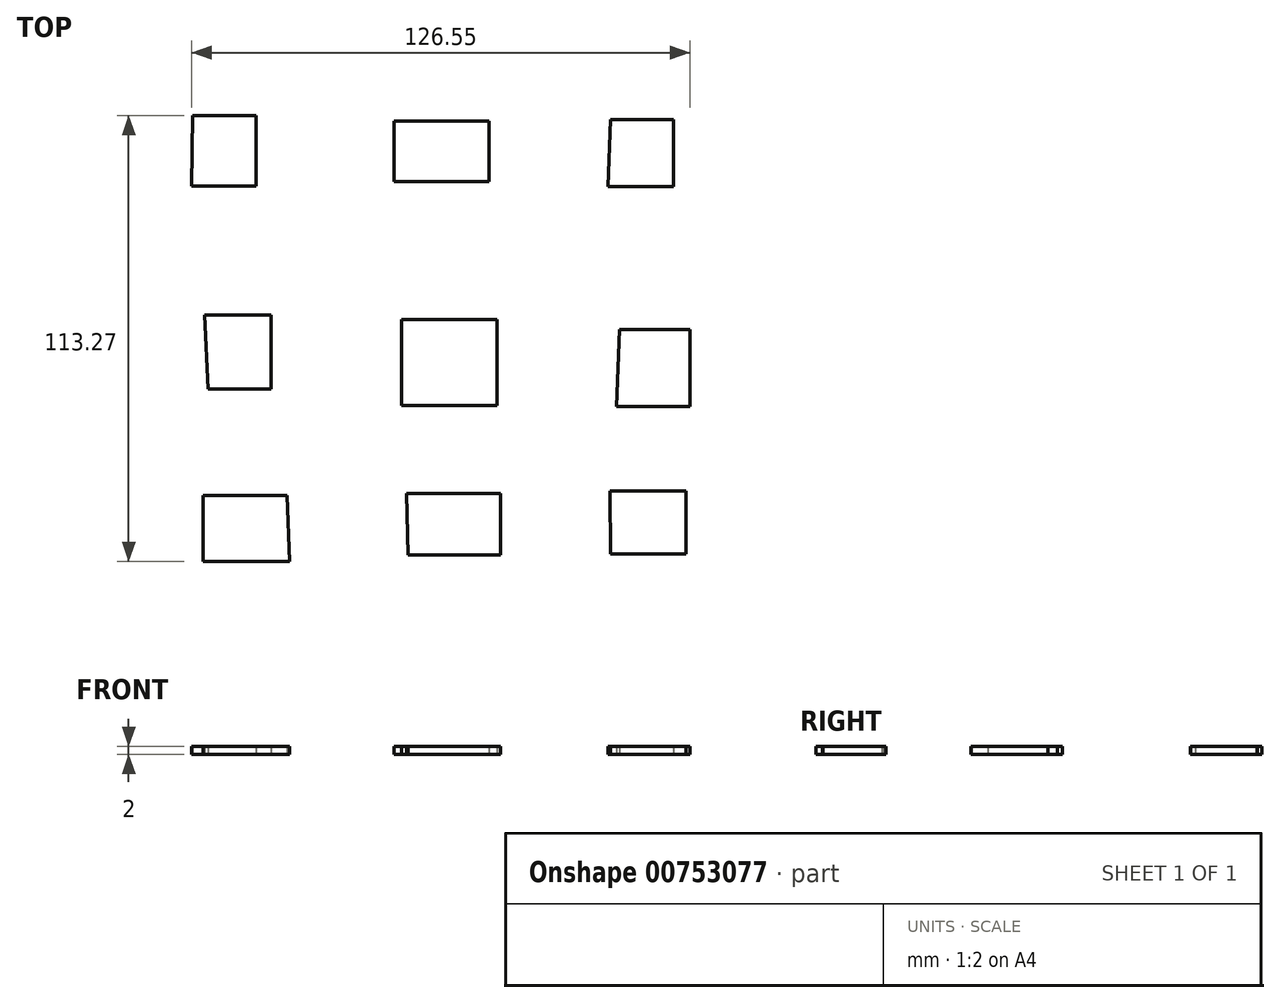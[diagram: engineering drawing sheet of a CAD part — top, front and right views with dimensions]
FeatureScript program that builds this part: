
annotation { "Feature Type Name" : "Feature", "Feature Type Description" : "" }
export const myFeature = defineFeature(function(context is Context, id is Id, definition is map)
    precondition{}
    {
        {
            var Q0;
            Q0=qCreatedBy(makeId("Top.planeOp"),FACE);
            var sketch = newSketch(context, id + "F0", { "sketchPlane" : qUnion([Q0])});
            skLineSegment(sketch, "E0", {"start": v(-64.52, 62.03) * mm, "end": v(-48.34, 62.03) * mm});
            skLineSegment(sketch, "E1", {"start": v(-48.34, 62.03) * mm, "end": v(-48.34, 44.19) * mm});
            skLineSegment(sketch, "E2", {"start": v(-48.34, 44.19) * mm, "end": v(-64.73, 44.19) * mm});
            skLineSegment(sketch, "E3", {"start": v(-64.73, 44.19) * mm, "end": v(-64.52, 62.03) * mm});
            skLineSegment(sketch, "E4", {"start": v(41.7, 61) * mm, "end": v(57.67, 61) * mm});
            skLineSegment(sketch, "E5", {"start": v(57.67, 61) * mm, "end": v(57.67, 43.98) * mm});
            skLineSegment(sketch, "E6", {"start": v(57.67, 43.98) * mm, "end": v(41.08, 43.98) * mm});
            skLineSegment(sketch, "E7", {"start": v(41.08, 43.98) * mm, "end": v(41.7, 61) * mm});
            skLineSegment(sketch, "E8", {"start": v(-13.28, 60.58) * mm, "end": v(10.79, 60.58) * mm});
            skLineSegment(sketch, "E9", {"start": v(10.79, 60.58) * mm, "end": v(10.79, 45.23) * mm});
            skLineSegment(sketch, "E10", {"start": v(10.79, 45.23) * mm, "end": v(-13.28, 45.23) * mm});
            skLineSegment(sketch, "E11", {"start": v(-13.28, 45.23) * mm, "end": v(-13.28, 60.58) * mm});
            skLineSegment(sketch, "E12", {"start": v(-40.45, -34.44) * mm, "end": v(-61.82, -34.44) * mm});
            skLineSegment(sketch, "E13", {"start": v(-61.82, -34.44) * mm, "end": v(-61.82, -51.24) * mm});
            skLineSegment(sketch, "E14", {"start": v(-61.82, -51.24) * mm, "end": v(-39.83, -51.24) * mm});
            skLineSegment(sketch, "E15", {"start": v(-39.83, -51.24) * mm, "end": v(-40.45, -34.44) * mm});
            skLineSegment(sketch, "E16", {"start": v(-10.17, -34.02) * mm, "end": v(13.7, -34.02) * mm});
            skLineSegment(sketch, "E17", {"start": v(13.7, -34.02) * mm, "end": v(13.7, -49.58) * mm});
            skLineSegment(sketch, "E18", {"start": v(13.7, -49.58) * mm, "end": v(-9.75, -49.58) * mm});
            skLineSegment(sketch, "E19", {"start": v(-9.75, -49.58) * mm, "end": v(-10.17, -34.02) * mm});
            skLineSegment(sketch, "E20", {"start": v(41.5, -33.4) * mm, "end": v(60.78, -33.4) * mm});
            skLineSegment(sketch, "E21", {"start": v(60.78, -33.4) * mm, "end": v(60.78, -49.37) * mm});
            skLineSegment(sketch, "E22", {"start": v(60.78, -49.37) * mm, "end": v(41.7, -49.37) * mm});
            skLineSegment(sketch, "E23", {"start": v(41.7, -49.37) * mm, "end": v(41.5, -33.4) * mm});
            skLineSegment(sketch, "E24", {"start": v(-11.41, 10.17) * mm, "end": v(12.86, 10.17) * mm});
            skLineSegment(sketch, "E25", {"start": v(12.86, 10.17) * mm, "end": v(12.86, -11.62) * mm});
            skLineSegment(sketch, "E26", {"start": v(12.86, -11.62) * mm, "end": v(-11.41, -11.62) * mm});
            skLineSegment(sketch, "E27", {"start": v(-11.41, -11.62) * mm, "end": v(-11.41, 10.17) * mm});
            skLineSegment(sketch, "E28", {"start": v(-61.4, 11.41) * mm, "end": v(-44.6, 11.41) * mm});
            skLineSegment(sketch, "E29", {"start": v(-44.6, 11.41) * mm, "end": v(-44.6, -7.47) * mm});
            skLineSegment(sketch, "E30", {"start": v(-44.6, -7.47) * mm, "end": v(-60.58, -7.47) * mm});
            skLineSegment(sketch, "E31", {"start": v(-60.58, -7.47) * mm, "end": v(-61.4, 11.41) * mm});
            skLineSegment(sketch, "E32", {"start": v(43.98, 7.68) * mm, "end": v(61.82, 7.68) * mm});
            skLineSegment(sketch, "E33", {"start": v(61.82, 7.68) * mm, "end": v(61.82, -11.83) * mm});
            skLineSegment(sketch, "E34", {"start": v(61.82, -11.83) * mm, "end": v(43.15, -11.83) * mm});
            skLineSegment(sketch, "E35", {"start": v(43.15, -11.83) * mm, "end": v(43.98, 7.68) * mm});
            skSolve(sketch);
        }
        {
            var Q0;
            Q0=makeQuery(id+"F0.imprint","IMPRINT",FACE,{"disambiguationData":[TD([[makeQuery(id+"F0.imprint","IMPRINT",EDGE,{"derivedFrom":sQuery(id+"F0.wireOp",EDGE,"E32")}),-1.0]])]});
            var Q1;
            Q1=makeQuery(id+"F0.imprint","IMPRINT",FACE,{"disambiguationData":[TD([[makeQuery(id+"F0.imprint","IMPRINT",EDGE,{"derivedFrom":sQuery(id+"F0.wireOp",EDGE,"E24")}),-1.0]])]});
            var Q2;
            Q2=makeQuery(id+"F0.imprint","IMPRINT",FACE,{"disambiguationData":[TD([[makeQuery(id+"F0.imprint","IMPRINT",EDGE,{"derivedFrom":sQuery(id+"F0.wireOp",EDGE,"E12")}),1.0]])]});
            var Q3;
            Q3=makeQuery(id+"F0.imprint","IMPRINT",FACE,{"disambiguationData":[TD([[makeQuery(id+"F0.imprint","IMPRINT",EDGE,{"derivedFrom":sQuery(id+"F0.wireOp",EDGE,"E8")}),-1.0]])]});
            var Q4;
            Q4=makeQuery(id+"F0.imprint","IMPRINT",FACE,{"disambiguationData":[TD([[makeQuery(id+"F0.imprint","IMPRINT",EDGE,{"derivedFrom":sQuery(id+"F0.wireOp",EDGE,"E16")}),-1.0]])]});
            var Q5;
            Q5=makeQuery(id+"F0.imprint","IMPRINT",FACE,{"disambiguationData":[TD([[makeQuery(id+"F0.imprint","IMPRINT",EDGE,{"derivedFrom":sQuery(id+"F0.wireOp",EDGE,"E0")}),-1.0]])]});
            var Q6;
            Q6=makeQuery(id+"F0.imprint","IMPRINT",FACE,{"disambiguationData":[TD([[makeQuery(id+"F0.imprint","IMPRINT",EDGE,{"derivedFrom":sQuery(id+"F0.wireOp",EDGE,"E4")}),-1.0]])]});
            var Q7;
            Q7=makeQuery(id+"F0.imprint","IMPRINT",FACE,{"disambiguationData":[TD([[makeQuery(id+"F0.imprint","IMPRINT",EDGE,{"derivedFrom":sQuery(id+"F0.wireOp",EDGE,"E28")}),-1.0]])]});
            var Q8;
            Q8=makeQuery(id+"F0.imprint","IMPRINT",FACE,{"disambiguationData":[TD([[makeQuery(id+"F0.imprint","IMPRINT",EDGE,{"derivedFrom":sQuery(id+"F0.wireOp",EDGE,"E20")}),-1.0]])]});
            extrude(context, id + "F1", {"entities" : qUnion([Q0, Q1, Q2, Q3, Q4, Q5, Q6, Q7, Q8]), "depth" : 2 * mm, "offsetDistance" : 25.4 * mm});
        }
    });
